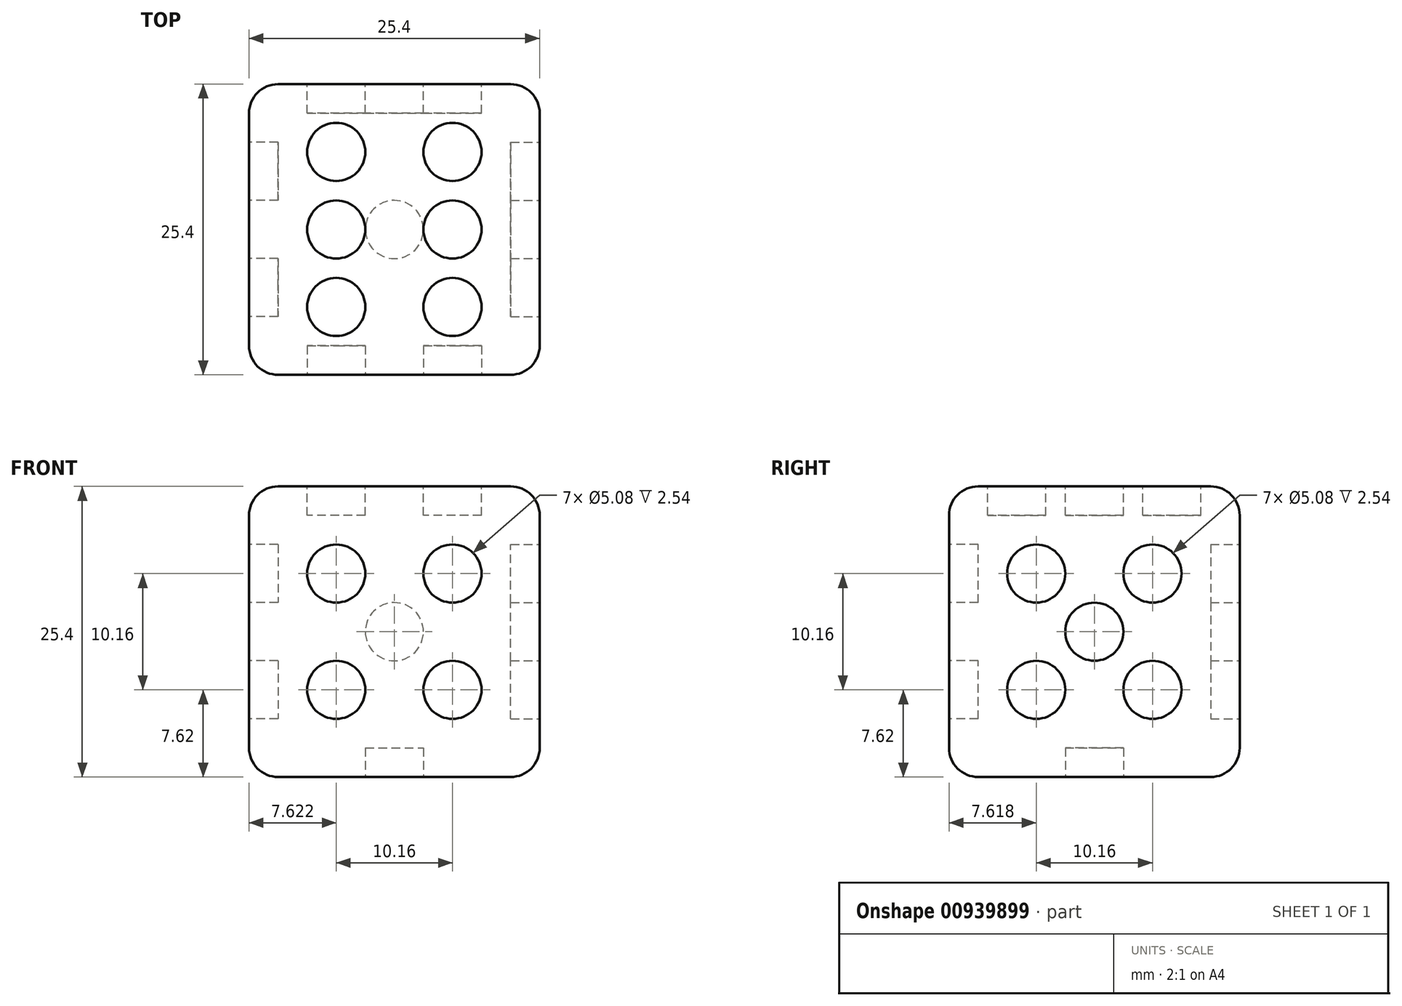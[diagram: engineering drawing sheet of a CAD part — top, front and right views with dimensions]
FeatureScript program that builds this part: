
annotation { "Feature Type Name" : "Feature", "Feature Type Description" : "" }
export const myFeature = defineFeature(function(context is Context, id is Id, definition is map)
    precondition{}
    {
        {
            var Q0;
            Q0=qCreatedBy(makeId("Top.planeOp"),FACE);
            var sketch = newSketch(context, id + "F0", { "sketchPlane" : qUnion([Q0])});
            skLineSegment(sketch, "E0.bottom", {"start": v(-52.85, 44.08) * mm, "end": v(-27.45, 44.08) * mm});
            skLineSegment(sketch, "E0.top", {"start": v(-52.85, 18.68) * mm, "end": v(-27.45, 18.68) * mm});
            skLineSegment(sketch, "E0.left", {"start": v(-52.85, 44.08) * mm, "end": v(-52.85, 18.68) * mm});
            skLineSegment(sketch, "E0.right", {"start": v(-27.45, 44.08) * mm, "end": v(-27.45, 18.68) * mm});
            skSolve(sketch);
        }
        {
            var Q0;
            Q0=makeQuery(id+"F0.imprint","IMPRINT",FACE,{"disambiguationData":[TD([[makeQuery(id+"F0.imprint","IMPRINT",EDGE,{"derivedFrom":sQuery(id+"F0.wireOp",EDGE,"E0.bottom")}),-1.0]])]});
            extrude(context, id + "F1", {"entities" : qUnion([Q0]), "depth" : 12.7 * mm, "offsetDistance" : 25.4 * mm});
        }
        {
            var Q0;
            Q0=makeQuery(id+"F1.opExtrude","CAP_FACE",FACE,{"disambiguationData":[OSD([sQuery(id+"F0.wireOp",EDGE,"E0.bottom"),sQuery(id+"F0.wireOp",EDGE,"E0.top"),sQuery(id+"F0.wireOp",EDGE,"E0.left"),sQuery(id+"F0.wireOp",EDGE,"E0.right")])],"isStart":false});
            var sketch = newSketch(context, id + "F2", { "sketchPlane" : qUnion([Q0])});
            skLineSegment(sketch, "E1.bottom", {"start": v(-49.04, 40.27) * mm, "end": v(-31.26, 40.27) * mm});
            skLineSegment(sketch, "E1.top", {"start": v(-49.04, 22.49) * mm, "end": v(-31.26, 22.49) * mm});
            skLineSegment(sketch, "E1.left", {"start": v(-49.04, 40.27) * mm, "end": v(-49.04, 22.49) * mm});
            skLineSegment(sketch, "E1.right", {"start": v(-31.26, 40.27) * mm, "end": v(-31.26, 22.49) * mm});
            skLineSegment(sketch, "E2.bottom", {"start": v(-52.85, 44.08) * mm, "end": v(-27.45, 44.08) * mm});
            skLineSegment(sketch, "E2.top", {"start": v(-52.85, 18.68) * mm, "end": v(-27.45, 18.68) * mm});
            skLineSegment(sketch, "E2.left", {"start": v(-52.85, 44.08) * mm, "end": v(-52.85, 18.68) * mm});
            skLineSegment(sketch, "E2.right", {"start": v(-27.45, 44.08) * mm, "end": v(-27.45, 18.68) * mm});
            skSolve(sketch);
        }
        {
            var Q0;
            Q0=makeQuery(id+"F2.imprint","IMPRINT",FACE,{"disambiguationData":[TD([[makeQuery(id+"F2.imprint","IMPRINT",EDGE,{"derivedFrom":sQuery(id+"F2.wireOp",EDGE,"E1.bottom")}),1.0]])]});
            var Q1;
            Q1=makeQuery(id+"F2.imprint","IMPRINT",FACE,{"disambiguationData":[TD([[makeQuery(id+"F2.imprint","IMPRINT",EDGE,{"derivedFrom":sQuery(id+"F2.wireOp",EDGE,"E1.bottom")}),-1.0]])]});
            extrude(context, id + "F3", {"entities" : qUnion([Q0, Q1]), "operationType" : NewBodyOperationType.ADD, "depth" : 8.9 * mm, "offsetDistance" : 25.4 * mm});
        }
        {
            var Q0;
            Q0=makeQuery(id+"F3.opExtrude","CAP_FACE",FACE,{"disambiguationData":[OSD([sQuery(id+"F2.wireOp",EDGE,"E1.bottom"),sQuery(id+"F2.wireOp",EDGE,"E1.top"),sQuery(id+"F2.wireOp",EDGE,"E1.left"),sQuery(id+"F2.wireOp",EDGE,"E1.right"),sQuery(id+"F2.wireOp",EDGE,"E2.bottom"),sQuery(id+"F2.wireOp",EDGE,"E2.top"),sQuery(id+"F2.wireOp",EDGE,"E2.left"),sQuery(id+"F2.wireOp",EDGE,"E2.right")])],"isStart":false});
            var sketch = newSketch(context, id + "F4", { "sketchPlane" : qUnion([Q0])});
            skLineSegment(sketch, "E3.bottom", {"start": v(-52.85, 44.08) * mm, "end": v(-27.45, 44.08) * mm});
            skLineSegment(sketch, "E3.top", {"start": v(-52.85, 18.68) * mm, "end": v(-27.45, 18.68) * mm});
            skLineSegment(sketch, "E3.left", {"start": v(-52.85, 44.08) * mm, "end": v(-52.85, 18.68) * mm});
            skLineSegment(sketch, "E3.right", {"start": v(-27.45, 44.08) * mm, "end": v(-27.45, 18.68) * mm});
            skSolve(sketch);
        }
        {
            var Q0;
            Q0=qSketchRegion(id+"F4",true);
            extrude(context, id + "F5", {"entities" : qUnion([Q0]), "operationType" : NewBodyOperationType.ADD, "depth" : 3.8 * mm, "offsetDistance" : 25.4 * mm});
        }
        {
            var Q0;
            Q0=makeQuery(id+"F5.opExtrude","CAP_EDGE",EDGE,{"disambiguationData":[OSD([sQuery(id+"F4.wireOp",EDGE,"E3.top")])],"isStart":false});
            var Q1;
            Q1=makeQuery(id+"F5.opExtrude","CAP_EDGE",EDGE,{"disambiguationData":[OSD([sQuery(id+"F4.wireOp",EDGE,"E3.right")])],"isStart":false});
            var Q2;
            Q2=makeQuery(id+"F5.boolean.opBoolean","MERGE",EDGE,{"derivedFrom":[makeQuery(id+"F3.boolean.opBoolean","MERGE",EDGE,{"derivedFrom":[makeQuery(id+"F1.opExtrude","SWEPT_EDGE",EDGE,{"disambiguationData":[OSD([sQuery(id+"F0.wireOp",EDGE,"E0.top"),sQuery(id+"F0.wireOp",EDGE,"E0.right")])]}),makeQuery(id+"F3.opExtrude","SWEPT_EDGE",EDGE,{"disambiguationData":[OSD([sQuery(id+"F2.wireOp",EDGE,"E2.top"),sQuery(id+"F2.wireOp",EDGE,"E2.right")])]})]}),makeQuery(id+"F5.opExtrude","SWEPT_EDGE",EDGE,{"disambiguationData":[OSD([sQuery(id+"F4.wireOp",EDGE,"E3.top"),sQuery(id+"F4.wireOp",EDGE,"E3.right")])]})]});
            var Q3;
            Q3=makeQuery(id+"F5.boolean.opBoolean","MERGE",EDGE,{"derivedFrom":[makeQuery(id+"F3.boolean.opBoolean","MERGE",EDGE,{"derivedFrom":[makeQuery(id+"F1.opExtrude","SWEPT_EDGE",EDGE,{"disambiguationData":[OSD([sQuery(id+"F0.wireOp",EDGE,"E0.bottom"),sQuery(id+"F0.wireOp",EDGE,"E0.right")])]}),makeQuery(id+"F3.opExtrude","SWEPT_EDGE",EDGE,{"disambiguationData":[OSD([sQuery(id+"F2.wireOp",EDGE,"E2.bottom"),sQuery(id+"F2.wireOp",EDGE,"E2.right")])]})]}),makeQuery(id+"F5.opExtrude","SWEPT_EDGE",EDGE,{"disambiguationData":[OSD([sQuery(id+"F4.wireOp",EDGE,"E3.bottom"),sQuery(id+"F4.wireOp",EDGE,"E3.right")])]})]});
            var Q4;
            Q4=makeQuery(id+"F5.opExtrude","CAP_EDGE",EDGE,{"disambiguationData":[OSD([sQuery(id+"F4.wireOp",EDGE,"E3.bottom")])],"isStart":false});
            var Q5;
            Q5=makeQuery(id+"F5.opExtrude","CAP_EDGE",EDGE,{"disambiguationData":[OSD([sQuery(id+"F4.wireOp",EDGE,"E3.left")])],"isStart":false});
            var Q6;
            Q6=makeQuery(id+"F5.boolean.opBoolean","MERGE",EDGE,{"derivedFrom":[makeQuery(id+"F3.boolean.opBoolean","MERGE",EDGE,{"derivedFrom":[makeQuery(id+"F1.opExtrude","SWEPT_EDGE",EDGE,{"disambiguationData":[OSD([sQuery(id+"F0.wireOp",EDGE,"E0.top"),sQuery(id+"F0.wireOp",EDGE,"E0.left")])]}),makeQuery(id+"F3.opExtrude","SWEPT_EDGE",EDGE,{"disambiguationData":[OSD([sQuery(id+"F2.wireOp",EDGE,"E2.top"),sQuery(id+"F2.wireOp",EDGE,"E2.left")])]})]}),makeQuery(id+"F5.opExtrude","SWEPT_EDGE",EDGE,{"disambiguationData":[OSD([sQuery(id+"F4.wireOp",EDGE,"E3.top"),sQuery(id+"F4.wireOp",EDGE,"E3.left")])]})]});
            var Q7;
            Q7=makeQuery(id+"F1.opExtrude","CAP_EDGE",EDGE,{"disambiguationData":[OSD([sQuery(id+"F0.wireOp",EDGE,"E0.top")])],"isStart":true});
            var Q8;
            Q8=makeQuery(id+"F1.opExtrude","CAP_EDGE",EDGE,{"disambiguationData":[OSD([sQuery(id+"F0.wireOp",EDGE,"E0.left")])],"isStart":true});
            var Q9;
            Q9=makeQuery(id+"F1.opExtrude","CAP_EDGE",EDGE,{"disambiguationData":[OSD([sQuery(id+"F0.wireOp",EDGE,"E0.bottom")])],"isStart":true});
            var Q10;
            Q10=makeQuery(id+"F1.opExtrude","CAP_EDGE",EDGE,{"disambiguationData":[OSD([sQuery(id+"F0.wireOp",EDGE,"E0.right")])],"isStart":true});
            var Q11;
            Q11=makeQuery(id+"F5.boolean.opBoolean","MERGE",EDGE,{"derivedFrom":[makeQuery(id+"F3.boolean.opBoolean","MERGE",EDGE,{"derivedFrom":[makeQuery(id+"F1.opExtrude","SWEPT_EDGE",EDGE,{"disambiguationData":[OSD([sQuery(id+"F0.wireOp",EDGE,"E0.bottom"),sQuery(id+"F0.wireOp",EDGE,"E0.left")])]}),makeQuery(id+"F3.opExtrude","SWEPT_EDGE",EDGE,{"disambiguationData":[OSD([sQuery(id+"F2.wireOp",EDGE,"E2.bottom"),sQuery(id+"F2.wireOp",EDGE,"E2.left")])]})]}),makeQuery(id+"F5.opExtrude","SWEPT_EDGE",EDGE,{"disambiguationData":[OSD([sQuery(id+"F4.wireOp",EDGE,"E3.bottom"),sQuery(id+"F4.wireOp",EDGE,"E3.left")])]})]});
            fillet(context, id + "F6", {"entities" : qUnion([Q0, Q1, Q2, Q3, Q4, Q5, Q6, Q7, Q8, Q9, Q10, Q11]), "radius" : 2.54 * mm, "tangentPropagation" : true, "allowEdgeOverflow" : false});
        }
        {
            var Q0;
            Q0=makeQuery(id+"F5.opExtrude","CAP_FACE",FACE,{"disambiguationData":[OSD([sQuery(id+"F4.wireOp",EDGE,"E3.bottom"),sQuery(id+"F4.wireOp",EDGE,"E3.top"),sQuery(id+"F4.wireOp",EDGE,"E3.left"),sQuery(id+"F4.wireOp",EDGE,"E3.right")])],"isStart":false});
            var sketch = newSketch(context, id + "F7", { "sketchPlane" : qUnion([Q0])});
            skLineSegment(sketch, "E4", {"start": v(-50.3, 41.54) * mm, "end": v(-45.23, 41.54) * mm});
            skLineSegment(sketch, "E5", {"start": v(-29.99, 41.54) * mm, "end": v(-29.99, 38.15) * mm});
            skLineSegment(sketch, "E6", {"start": v(-29.99, 21.22) * mm, "end": v(-35.07, 21.22) * mm});
            skLineSegment(sketch, "E7", {"start": v(-50.3, 21.22) * mm, "end": v(-50.3, 24.6) * mm});
            skLineSegment(sketch, "E8", {"start": v(-50.3, 24.6) * mm, "end": v(-45.23, 24.6) * mm});
            skLineSegment(sketch, "E9", {"start": v(-45.23, 41.54) * mm, "end": v(-45.23, 38.15) * mm});
            skLineSegment(sketch, "E10", {"start": v(-29.99, 38.15) * mm, "end": v(-35.07, 38.15) * mm});
            skLineSegment(sketch, "E11", {"start": v(-35.07, 21.22) * mm, "end": v(-35.07, 24.6) * mm});
            skLineSegment(sketch, "E12", {"start": v(-45.23, 38.15) * mm, "end": v(-45.23, 31.38) * mm});
            skLineSegment(sketch, "E13", {"start": v(-35.07, 38.15) * mm, "end": v(-35.07, 31.38) * mm});
            skCircle(sketch, "E14", {"center": v(-45.23, 38.15) * mm, "radius": 2.54 * mm});
            skCircle(sketch, "E15", {"center": v(-45.23, 31.38) * mm, "radius": 2.54 * mm});
            skCircle(sketch, "E16", {"center": v(-45.23, 24.6) * mm, "radius": 2.54 * mm});
            skCircle(sketch, "E17", {"center": v(-35.07, 24.6) * mm, "radius": 2.54 * mm});
            skCircle(sketch, "E18", {"center": v(-35.07, 31.38) * mm, "radius": 2.54 * mm});
            skCircle(sketch, "E19", {"center": v(-35.07, 38.15) * mm, "radius": 2.54 * mm});
            skSolve(sketch);
        }
        {
            var Q0;
            {var subQ0=sQuery(id+"F7.wireOp",EDGE,"E12");var subQ1=sQuery(id+"F7.wireOp",EDGE,"E9");var subQ2=makeQuery(id+"F7.imprint","INTERSECT",VERTEX,{"derivedFrom":[subQ1,subQ0]});Q0=makeQuery(id+"F7.imprint","IMPRINT",FACE,{"disambiguationData":[TD([[makeQuery(id+"F7.imprint","IMPRINT",EDGE,{"disambiguationData":[TD([[subQ2,1.0]])],"derivedFrom":subQ1}),1.0]])]});}
            var Q1;
            {var subQ0=sQuery(id+"F7.wireOp",EDGE,"E12");var subQ1=sQuery(id+"F7.wireOp",EDGE,"E9");var subQ2=makeQuery(id+"F7.imprint","INTERSECT",VERTEX,{"derivedFrom":[subQ1,subQ0]});Q1=makeQuery(id+"F7.imprint","IMPRINT",FACE,{"disambiguationData":[TD([[makeQuery(id+"F7.imprint","IMPRINT",EDGE,{"disambiguationData":[TD([[subQ2,1.0]])],"derivedFrom":subQ1}),-1.0]])]});}
            var Q2;
            {var subQ0=sQuery(id+"F7.wireOp",EDGE,"E13");var subQ1=sQuery(id+"F7.wireOp",EDGE,"E10");var subQ2=makeQuery(id+"F7.imprint","INTERSECT",VERTEX,{"derivedFrom":[subQ1,subQ0]});Q2=makeQuery(id+"F7.imprint","IMPRINT",FACE,{"disambiguationData":[TD([[makeQuery(id+"F7.imprint","IMPRINT",EDGE,{"disambiguationData":[TD([[subQ2,1.0]])],"derivedFrom":subQ1}),-1.0]])]});}
            var Q3;
            {var subQ0=sQuery(id+"F7.wireOp",EDGE,"E13");var subQ1=sQuery(id+"F7.wireOp",EDGE,"E10");var subQ2=makeQuery(id+"F7.imprint","INTERSECT",VERTEX,{"derivedFrom":[subQ1,subQ0]});Q3=makeQuery(id+"F7.imprint","IMPRINT",FACE,{"disambiguationData":[TD([[makeQuery(id+"F7.imprint","IMPRINT",EDGE,{"disambiguationData":[TD([[subQ2,1.0]])],"derivedFrom":subQ1}),1.0]])]});}
            var Q4;
            Q4=makeQuery(id+"F7.imprint","IMPRINT",FACE,{"disambiguationData":[TD([[makeQuery(id+"F7.imprint","IMPRINT",EDGE,{"derivedFrom":sQuery(id+"F7.wireOp",EDGE,"E18")}),1.0]])]});
            var Q5;
            Q5=makeQuery(id+"F7.imprint","IMPRINT",FACE,{"disambiguationData":[TD([[makeQuery(id+"F7.imprint","IMPRINT",EDGE,{"derivedFrom":sQuery(id+"F7.wireOp",EDGE,"E17")}),1.0]])]});
            var Q6;
            Q6=makeQuery(id+"F7.imprint","IMPRINT",FACE,{"disambiguationData":[TD([[makeQuery(id+"F7.imprint","IMPRINT",EDGE,{"derivedFrom":sQuery(id+"F7.wireOp",EDGE,"E16")}),1.0]])]});
            var Q7;
            Q7=makeQuery(id+"F7.imprint","IMPRINT",FACE,{"disambiguationData":[TD([[makeQuery(id+"F7.imprint","IMPRINT",EDGE,{"derivedFrom":sQuery(id+"F7.wireOp",EDGE,"E15")}),1.0]])]});
            extrude(context, id + "F8", {"entities" : qUnion([Q0, Q1, Q2, Q3, Q4, Q5, Q6, Q7]), "operationType" : NewBodyOperationType.REMOVE, "oppositeDirection" : true, "depth" : 2.54 * mm, "offsetDistance" : 25.4 * mm});
        }
        {
            var Q0;
            Q0=makeQuery(id+"F5.boolean.opBoolean","MERGE",FACE,{"derivedFrom":[makeQuery(id+"F3.boolean.opBoolean","MERGE",FACE,{"derivedFrom":[makeQuery(id+"F1.opExtrude","SWEPT_FACE",FACE,{"disambiguationData":[OSD([sQuery(id+"F0.wireOp",EDGE,"E0.right")])]}),makeQuery(id+"F3.opExtrude","SWEPT_FACE",FACE,{"disambiguationData":[OSD([sQuery(id+"F2.wireOp",EDGE,"E2.right")])]})]}),makeQuery(id+"F5.opExtrude","SWEPT_FACE",FACE,{"disambiguationData":[OSD([sQuery(id+"F4.wireOp",EDGE,"E3.right")])]})]});
            var sketch = newSketch(context, id + "F9", { "sketchPlane" : qUnion([Q0])});
            skLineSegment(sketch, "E20", {"start": v(21.22, 22.86) * mm, "end": v(31.38, 22.86) * mm});
            skLineSegment(sketch, "E21", {"start": v(41.54, 22.86) * mm, "end": v(41.54, 12.7) * mm});
            skLineSegment(sketch, "E22", {"start": v(41.54, 12.7) * mm, "end": v(31.38, 12.7) * mm});
            skCircle(sketch, "E23", {"center": v(31.38, 12.7) * mm, "radius": 2.54 * mm});
            skLineSegment(sketch, "E24", {"start": v(21.22, 22.86) * mm, "end": v(26.3, 22.86) * mm});
            skLineSegment(sketch, "E25", {"start": v(26.3, 22.86) * mm, "end": v(26.3, 17.78) * mm});
            skCircle(sketch, "E26", {"center": v(26.3, 17.78) * mm, "radius": 2.54 * mm});
            skLineSegment(sketch, "E27", {"start": v(26.3, 17.78) * mm, "end": v(26.3, 7.62) * mm});
            skCircle(sketch, "E28", {"center": v(26.3, 7.62) * mm, "radius": 2.54 * mm});
            skLineSegment(sketch, "E29", {"start": v(41.54, 22.86) * mm, "end": v(41.54, 17.78) * mm});
            skLineSegment(sketch, "E30", {"start": v(41.54, 17.78) * mm, "end": v(36.46, 17.78) * mm});
            skCircle(sketch, "E31", {"center": v(36.46, 17.78) * mm, "radius": 2.54 * mm});
            skLineSegment(sketch, "E32", {"start": v(36.46, 17.78) * mm, "end": v(36.46, 7.62) * mm});
            skCircle(sketch, "E33", {"center": v(36.46, 7.62) * mm, "radius": 2.54 * mm});
            skSolve(sketch);
        }
        {
            var Q0;
            {var subQ0=sQuery(id+"F9.wireOp",EDGE,"E27");var subQ1=sQuery(id+"F9.wireOp",EDGE,"E25");var subQ2=makeQuery(id+"F9.imprint","INTERSECT",VERTEX,{"derivedFrom":[subQ1,subQ0]});Q0=makeQuery(id+"F9.imprint","IMPRINT",FACE,{"disambiguationData":[TD([[makeQuery(id+"F9.imprint","IMPRINT",EDGE,{"disambiguationData":[TD([[subQ2,1.0]])],"derivedFrom":subQ1}),1.0]])]});}
            var Q1;
            {var subQ0=sQuery(id+"F9.wireOp",EDGE,"E27");var subQ1=sQuery(id+"F9.wireOp",EDGE,"E25");var subQ2=makeQuery(id+"F9.imprint","INTERSECT",VERTEX,{"derivedFrom":[subQ1,subQ0]});Q1=makeQuery(id+"F9.imprint","IMPRINT",FACE,{"disambiguationData":[TD([[makeQuery(id+"F9.imprint","IMPRINT",EDGE,{"disambiguationData":[TD([[subQ2,1.0]])],"derivedFrom":subQ1}),-1.0]])]});}
            var Q2;
            Q2=makeQuery(id+"F9.imprint","IMPRINT",FACE,{"disambiguationData":[TD([[makeQuery(id+"F9.imprint","IMPRINT",EDGE,{"derivedFrom":sQuery(id+"F9.wireOp",EDGE,"E28")}),1.0]])]});
            var Q3;
            Q3=makeQuery(id+"F9.imprint","IMPRINT",FACE,{"disambiguationData":[TD([[makeQuery(id+"F9.imprint","IMPRINT",EDGE,{"derivedFrom":sQuery(id+"F9.wireOp",EDGE,"E23")}),1.0]])]});
            var Q4;
            {var subQ0=sQuery(id+"F9.wireOp",EDGE,"E32");var subQ1=sQuery(id+"F9.wireOp",EDGE,"E30");var subQ2=makeQuery(id+"F9.imprint","INTERSECT",VERTEX,{"derivedFrom":[subQ1,subQ0]});Q4=makeQuery(id+"F9.imprint","IMPRINT",FACE,{"disambiguationData":[TD([[makeQuery(id+"F9.imprint","IMPRINT",EDGE,{"disambiguationData":[TD([[subQ2,1.0]])],"derivedFrom":subQ1}),-1.0]])]});}
            var Q5;
            {var subQ0=sQuery(id+"F9.wireOp",EDGE,"E32");var subQ1=sQuery(id+"F9.wireOp",EDGE,"E30");var subQ2=makeQuery(id+"F9.imprint","INTERSECT",VERTEX,{"derivedFrom":[subQ1,subQ0]});Q5=makeQuery(id+"F9.imprint","IMPRINT",FACE,{"disambiguationData":[TD([[makeQuery(id+"F9.imprint","IMPRINT",EDGE,{"disambiguationData":[TD([[subQ2,1.0]])],"derivedFrom":subQ1}),1.0]])]});}
            var Q6;
            Q6=makeQuery(id+"F9.imprint","IMPRINT",FACE,{"disambiguationData":[TD([[makeQuery(id+"F9.imprint","IMPRINT",EDGE,{"derivedFrom":sQuery(id+"F9.wireOp",EDGE,"E33")}),1.0]])]});
            extrude(context, id + "F10", {"entities" : qUnion([Q0, Q1, Q2, Q3, Q4, Q5, Q6]), "operationType" : NewBodyOperationType.REMOVE, "oppositeDirection" : true, "depth" : 2.54 * mm, "offsetDistance" : 25.4 * mm});
        }
        {
            var Q0;
            Q0=makeQuery(id+"F5.boolean.opBoolean","MERGE",FACE,{"derivedFrom":[makeQuery(id+"F3.boolean.opBoolean","MERGE",FACE,{"derivedFrom":[makeQuery(id+"F1.opExtrude","SWEPT_FACE",FACE,{"disambiguationData":[OSD([sQuery(id+"F0.wireOp",EDGE,"E0.bottom")])]}),makeQuery(id+"F3.opExtrude","SWEPT_FACE",FACE,{"disambiguationData":[OSD([sQuery(id+"F2.wireOp",EDGE,"E2.bottom")])]})]}),makeQuery(id+"F5.opExtrude","SWEPT_FACE",FACE,{"disambiguationData":[OSD([sQuery(id+"F4.wireOp",EDGE,"E3.bottom")])]})]});
            var sketch = newSketch(context, id + "F11", { "sketchPlane" : qUnion([Q0])});
            skLineSegment(sketch, "E34", {"start": v(29.99, 22.86) * mm, "end": v(40.15, 22.86) * mm});
            skLineSegment(sketch, "E35", {"start": v(40.15, 22.86) * mm, "end": v(40.15, 12.7) * mm});
            skCircle(sketch, "E36", {"center": v(40.15, 12.7) * mm, "radius": 2.54 * mm});
            skLineSegment(sketch, "E37", {"start": v(29.99, 22.86) * mm, "end": v(35.07, 22.86) * mm});
            skLineSegment(sketch, "E38", {"start": v(35.07, 22.86) * mm, "end": v(35.07, 17.78) * mm});
            skLineSegment(sketch, "E39", {"start": v(50.3, 2.54) * mm, "end": v(45.23, 2.54) * mm});
            skLineSegment(sketch, "E40", {"start": v(45.23, 2.54) * mm, "end": v(45.23, 7.62) * mm});
            skCircle(sketch, "E41", {"center": v(35.07, 17.78) * mm, "radius": 2.54 * mm});
            skCircle(sketch, "E42", {"center": v(45.23, 7.62) * mm, "radius": 2.54 * mm});
            skSolve(sketch);
        }
        {
            var Q0;
            Q0=makeQuery(id+"F11.imprint","IMPRINT",FACE,{"disambiguationData":[TD([[makeQuery(id+"F11.imprint","IMPRINT",EDGE,{"derivedFrom":sQuery(id+"F11.wireOp",EDGE,"E41")}),1.0]])]});
            var Q1;
            Q1=makeQuery(id+"F11.imprint","IMPRINT",FACE,{"disambiguationData":[TD([[makeQuery(id+"F11.imprint","IMPRINT",EDGE,{"derivedFrom":sQuery(id+"F11.wireOp",EDGE,"E36")}),1.0]])]});
            var Q2;
            Q2=makeQuery(id+"F11.imprint","IMPRINT",FACE,{"disambiguationData":[TD([[makeQuery(id+"F11.imprint","IMPRINT",EDGE,{"derivedFrom":sQuery(id+"F11.wireOp",EDGE,"E42")}),1.0]])]});
            extrude(context, id + "F12", {"entities" : qUnion([Q0, Q1, Q2]), "operationType" : NewBodyOperationType.REMOVE, "oppositeDirection" : true, "depth" : 2.54 * mm, "offsetDistance" : 25.4 * mm});
        }
        {
            var Q0;
            Q0=makeQuery(id+"F5.boolean.opBoolean","MERGE",FACE,{"derivedFrom":[makeQuery(id+"F3.boolean.opBoolean","MERGE",FACE,{"derivedFrom":[makeQuery(id+"F1.opExtrude","SWEPT_FACE",FACE,{"disambiguationData":[OSD([sQuery(id+"F0.wireOp",EDGE,"E0.left")])]}),makeQuery(id+"F3.opExtrude","SWEPT_FACE",FACE,{"disambiguationData":[OSD([sQuery(id+"F2.wireOp",EDGE,"E2.left")])]})]}),makeQuery(id+"F5.opExtrude","SWEPT_FACE",FACE,{"disambiguationData":[OSD([sQuery(id+"F4.wireOp",EDGE,"E3.left")])]})]});
            var sketch = newSketch(context, id + "F13", { "sketchPlane" : qUnion([Q0])});
            skLineSegment(sketch, "E43", {"start": v(-41.54, 22.86) * mm, "end": v(-36.46, 22.86) * mm});
            skLineSegment(sketch, "E44", {"start": v(-36.46, 22.86) * mm, "end": v(-36.46, 17.78) * mm});
            skLineSegment(sketch, "E45", {"start": v(-21.22, 2.54) * mm, "end": v(-26.3, 2.54) * mm});
            skLineSegment(sketch, "E46", {"start": v(-26.3, 2.54) * mm, "end": v(-26.3, 7.62) * mm});
            skCircle(sketch, "E47", {"center": v(-36.46, 17.78) * mm, "radius": 2.54 * mm});
            skCircle(sketch, "E48", {"center": v(-26.3, 7.62) * mm, "radius": 2.54 * mm});
            skSolve(sketch);
        }
        {
            var Q0;
            Q0=makeQuery(id+"F13.imprint","IMPRINT",FACE,{"disambiguationData":[TD([[makeQuery(id+"F13.imprint","IMPRINT",EDGE,{"derivedFrom":sQuery(id+"F13.wireOp",EDGE,"E47")}),1.0]])]});
            var Q1;
            Q1=makeQuery(id+"F13.imprint","IMPRINT",FACE,{"disambiguationData":[TD([[makeQuery(id+"F13.imprint","IMPRINT",EDGE,{"derivedFrom":sQuery(id+"F13.wireOp",EDGE,"E48")}),1.0]])]});
            extrude(context, id + "F14", {"entities" : qUnion([Q0, Q1]), "operationType" : NewBodyOperationType.REMOVE, "oppositeDirection" : true, "depth" : 2.54 * mm, "offsetDistance" : 25.4 * mm});
        }
        {
            var Q0;
            Q0=makeQuery(id+"F5.boolean.opBoolean","MERGE",FACE,{"derivedFrom":[makeQuery(id+"F3.boolean.opBoolean","MERGE",FACE,{"derivedFrom":[makeQuery(id+"F1.opExtrude","SWEPT_FACE",FACE,{"disambiguationData":[OSD([sQuery(id+"F0.wireOp",EDGE,"E0.top")])]}),makeQuery(id+"F3.opExtrude","SWEPT_FACE",FACE,{"disambiguationData":[OSD([sQuery(id+"F2.wireOp",EDGE,"E2.top")])]})]}),makeQuery(id+"F5.opExtrude","SWEPT_FACE",FACE,{"disambiguationData":[OSD([sQuery(id+"F4.wireOp",EDGE,"E3.top")])]})]});
            var sketch = newSketch(context, id + "F15", { "sketchPlane" : qUnion([Q0])});
            skLineSegment(sketch, "E49", {"start": v(-50.3, 22.86) * mm, "end": v(-45.23, 22.86) * mm});
            skLineSegment(sketch, "E50", {"start": v(-45.23, 22.86) * mm, "end": v(-45.23, 17.78) * mm});
            skLineSegment(sketch, "E51", {"start": v(-29.99, 22.86) * mm, "end": v(-29.99, 17.78) * mm});
            skLineSegment(sketch, "E52", {"start": v(-29.99, 17.78) * mm, "end": v(-35.07, 17.78) * mm});
            skLineSegment(sketch, "E53", {"start": v(-29.99, 2.54) * mm, "end": v(-35.07, 2.54) * mm});
            skLineSegment(sketch, "E54", {"start": v(-35.07, 2.54) * mm, "end": v(-35.07, 7.62) * mm});
            skLineSegment(sketch, "E55", {"start": v(-50.3, 2.54) * mm, "end": v(-45.23, 2.54) * mm});
            skLineSegment(sketch, "E56", {"start": v(-45.23, 2.54) * mm, "end": v(-45.23, 7.62) * mm});
            skCircle(sketch, "E57", {"center": v(-45.23, 17.78) * mm, "radius": 2.54 * mm});
            skCircle(sketch, "E58", {"center": v(-35.07, 17.78) * mm, "radius": 2.54 * mm});
            skCircle(sketch, "E59", {"center": v(-35.07, 7.62) * mm, "radius": 2.54 * mm});
            skCircle(sketch, "E60", {"center": v(-45.23, 7.62) * mm, "radius": 2.54 * mm});
            skSolve(sketch);
        }
        {
            var Q0;
            Q0=makeQuery(id+"F15.imprint","IMPRINT",FACE,{"disambiguationData":[TD([[makeQuery(id+"F15.imprint","IMPRINT",EDGE,{"derivedFrom":sQuery(id+"F15.wireOp",EDGE,"E57")}),1.0]])]});
            var Q1;
            Q1=makeQuery(id+"F15.imprint","IMPRINT",FACE,{"disambiguationData":[TD([[makeQuery(id+"F15.imprint","IMPRINT",EDGE,{"derivedFrom":sQuery(id+"F15.wireOp",EDGE,"E58")}),1.0]])]});
            var Q2;
            Q2=makeQuery(id+"F15.imprint","IMPRINT",FACE,{"disambiguationData":[TD([[makeQuery(id+"F15.imprint","IMPRINT",EDGE,{"derivedFrom":sQuery(id+"F15.wireOp",EDGE,"E59")}),1.0]])]});
            var Q3;
            Q3=makeQuery(id+"F15.imprint","IMPRINT",FACE,{"disambiguationData":[TD([[makeQuery(id+"F15.imprint","IMPRINT",EDGE,{"derivedFrom":sQuery(id+"F15.wireOp",EDGE,"E60")}),1.0]])]});
            extrude(context, id + "F16", {"entities" : qUnion([Q0, Q1, Q2, Q3]), "operationType" : NewBodyOperationType.REMOVE, "oppositeDirection" : true, "depth" : 2.54 * mm, "offsetDistance" : 25.4 * mm});
        }
        {
            var Q0;
            Q0=makeQuery(id+"F1.opExtrude","CAP_FACE",FACE,{"disambiguationData":[OSD([sQuery(id+"F0.wireOp",EDGE,"E0.bottom"),sQuery(id+"F0.wireOp",EDGE,"E0.top"),sQuery(id+"F0.wireOp",EDGE,"E0.left"),sQuery(id+"F0.wireOp",EDGE,"E0.right")])],"isStart":true});
            var sketch = newSketch(context, id + "F17", { "sketchPlane" : qUnion([Q0])});
            skLineSegment(sketch, "E61", {"start": v(-50.3, -21.22) * mm, "end": v(-40.15, -21.22) * mm});
            skLineSegment(sketch, "E62", {"start": v(-29.99, -21.22) * mm, "end": v(-29.99, -31.38) * mm});
            skLineSegment(sketch, "E63", {"start": v(-40.15, -21.22) * mm, "end": v(-40.15, -31.38) * mm});
            skCircle(sketch, "E64", {"center": v(-40.15, -31.38) * mm, "radius": 2.54 * mm});
            skSolve(sketch);
        }
        {
            var Q0;
            Q0=makeQuery(id+"F17.imprint","IMPRINT",FACE,{"disambiguationData":[TD([[makeQuery(id+"F17.imprint","IMPRINT",EDGE,{"derivedFrom":sQuery(id+"F17.wireOp",EDGE,"E64")}),1.0]])]});
            extrude(context, id + "F18", {"entities" : qUnion([Q0]), "operationType" : NewBodyOperationType.REMOVE, "oppositeDirection" : true, "depth" : 2.54 * mm, "offsetDistance" : 25.4 * mm});
        }
        {
            var Q0;
            Q0=makeQuery(id+"F11.imprint","IMPRINT",FACE,{"disambiguationData":[TD([[makeQuery(id+"F11.imprint","IMPRINT",EDGE,{"derivedFrom":sQuery(id+"F11.wireOp",EDGE,"E41")}),1.0]])]});
            var Q1;
            Q1=makeQuery(id+"F11.imprint","IMPRINT",FACE,{"disambiguationData":[TD([[makeQuery(id+"F11.imprint","IMPRINT",EDGE,{"derivedFrom":sQuery(id+"F11.wireOp",EDGE,"E36")}),1.0]])]});
            var Q2;
            Q2=makeQuery(id+"F11.imprint","IMPRINT",FACE,{"disambiguationData":[TD([[makeQuery(id+"F11.imprint","IMPRINT",EDGE,{"derivedFrom":sQuery(id+"F11.wireOp",EDGE,"E42")}),1.0]])]});
            extrude(context, id + "F19", {"entities" : qUnion([Q0, Q1, Q2]), "oppositeDirection" : true, "depth" : 2.54 * mm, "offsetDistance" : 25.4 * mm});
        }
        {
            var Q0;
            {var subQ0=sQuery(id+"F9.wireOp",EDGE,"E27");var subQ1=sQuery(id+"F9.wireOp",EDGE,"E25");var subQ2=makeQuery(id+"F9.imprint","INTERSECT",VERTEX,{"derivedFrom":[subQ1,subQ0]});Q0=makeQuery(id+"F9.imprint","IMPRINT",FACE,{"disambiguationData":[TD([[makeQuery(id+"F9.imprint","IMPRINT",EDGE,{"disambiguationData":[TD([[subQ2,1.0]])],"derivedFrom":subQ1}),1.0]])]});}
            var Q1;
            {var subQ0=sQuery(id+"F9.wireOp",EDGE,"E27");var subQ1=sQuery(id+"F9.wireOp",EDGE,"E25");var subQ2=makeQuery(id+"F9.imprint","INTERSECT",VERTEX,{"derivedFrom":[subQ1,subQ0]});Q1=makeQuery(id+"F9.imprint","IMPRINT",FACE,{"disambiguationData":[TD([[makeQuery(id+"F9.imprint","IMPRINT",EDGE,{"disambiguationData":[TD([[subQ2,1.0]])],"derivedFrom":subQ1}),-1.0]])]});}
            var Q2;
            {var subQ0=sQuery(id+"F9.wireOp",EDGE,"E32");var subQ1=sQuery(id+"F9.wireOp",EDGE,"E30");var subQ2=makeQuery(id+"F9.imprint","INTERSECT",VERTEX,{"derivedFrom":[subQ1,subQ0]});Q2=makeQuery(id+"F9.imprint","IMPRINT",FACE,{"disambiguationData":[TD([[makeQuery(id+"F9.imprint","IMPRINT",EDGE,{"disambiguationData":[TD([[subQ2,1.0]])],"derivedFrom":subQ1}),-1.0]])]});}
            var Q3;
            {var subQ0=sQuery(id+"F9.wireOp",EDGE,"E32");var subQ1=sQuery(id+"F9.wireOp",EDGE,"E30");var subQ2=makeQuery(id+"F9.imprint","INTERSECT",VERTEX,{"derivedFrom":[subQ1,subQ0]});Q3=makeQuery(id+"F9.imprint","IMPRINT",FACE,{"disambiguationData":[TD([[makeQuery(id+"F9.imprint","IMPRINT",EDGE,{"disambiguationData":[TD([[subQ2,1.0]])],"derivedFrom":subQ1}),1.0]])]});}
            var Q4;
            Q4=makeQuery(id+"F9.imprint","IMPRINT",FACE,{"disambiguationData":[TD([[makeQuery(id+"F9.imprint","IMPRINT",EDGE,{"derivedFrom":sQuery(id+"F9.wireOp",EDGE,"E28")}),1.0]])]});
            var Q5;
            Q5=makeQuery(id+"F9.imprint","IMPRINT",FACE,{"disambiguationData":[TD([[makeQuery(id+"F9.imprint","IMPRINT",EDGE,{"derivedFrom":sQuery(id+"F9.wireOp",EDGE,"E23")}),1.0]])]});
            var Q6;
            Q6=makeQuery(id+"F9.imprint","IMPRINT",FACE,{"disambiguationData":[TD([[makeQuery(id+"F9.imprint","IMPRINT",EDGE,{"derivedFrom":sQuery(id+"F9.wireOp",EDGE,"E33")}),1.0]])]});
            extrude(context, id + "F20", {"entities" : qUnion([Q0, Q1, Q2, Q3, Q4, Q5, Q6]), "oppositeDirection" : true, "depth" : 2.54 * mm, "offsetDistance" : 25.4 * mm});
        }
        {
            var Q0;
            Q0=makeQuery(id+"F13.imprint","IMPRINT",FACE,{"disambiguationData":[TD([[makeQuery(id+"F13.imprint","IMPRINT",EDGE,{"derivedFrom":sQuery(id+"F13.wireOp",EDGE,"E47")}),1.0]])]});
            var Q1;
            Q1=makeQuery(id+"F13.imprint","IMPRINT",FACE,{"disambiguationData":[TD([[makeQuery(id+"F13.imprint","IMPRINT",EDGE,{"derivedFrom":sQuery(id+"F13.wireOp",EDGE,"E48")}),1.0]])]});
            extrude(context, id + "F21", {"entities" : qUnion([Q0, Q1]), "oppositeDirection" : true, "depth" : 2.54 * mm, "offsetDistance" : 25.4 * mm});
        }
        {
            var Q0;
            Q0=makeQuery(id+"F15.imprint","IMPRINT",FACE,{"disambiguationData":[TD([[makeQuery(id+"F15.imprint","IMPRINT",EDGE,{"derivedFrom":sQuery(id+"F15.wireOp",EDGE,"E57")}),1.0]])]});
            var Q1;
            Q1=makeQuery(id+"F15.imprint","IMPRINT",FACE,{"disambiguationData":[TD([[makeQuery(id+"F15.imprint","IMPRINT",EDGE,{"derivedFrom":sQuery(id+"F15.wireOp",EDGE,"E58")}),1.0]])]});
            var Q2;
            Q2=makeQuery(id+"F15.imprint","IMPRINT",FACE,{"disambiguationData":[TD([[makeQuery(id+"F15.imprint","IMPRINT",EDGE,{"derivedFrom":sQuery(id+"F15.wireOp",EDGE,"E59")}),1.0]])]});
            var Q3;
            Q3=makeQuery(id+"F15.imprint","IMPRINT",FACE,{"disambiguationData":[TD([[makeQuery(id+"F15.imprint","IMPRINT",EDGE,{"derivedFrom":sQuery(id+"F15.wireOp",EDGE,"E60")}),1.0]])]});
            extrude(context, id + "F22", {"entities" : qUnion([Q0, Q1, Q2, Q3]), "oppositeDirection" : true, "depth" : 2.54 * mm, "offsetDistance" : 25.4 * mm});
        }
        {
            var Q0;
            Q0=makeQuery(id+"F17.imprint","IMPRINT",FACE,{"disambiguationData":[TD([[makeQuery(id+"F17.imprint","IMPRINT",EDGE,{"derivedFrom":sQuery(id+"F17.wireOp",EDGE,"E64")}),1.0]])]});
            extrude(context, id + "F23", {"entities" : qUnion([Q0]), "oppositeDirection" : true, "depth" : 2.54 * mm, "offsetDistance" : 25.4 * mm});
        }
        {
            var Q0;
            {var subQ0=sQuery(id+"F7.wireOp",EDGE,"E12");var subQ1=sQuery(id+"F7.wireOp",EDGE,"E9");var subQ2=makeQuery(id+"F7.imprint","INTERSECT",VERTEX,{"derivedFrom":[subQ1,subQ0]});Q0=makeQuery(id+"F7.imprint","IMPRINT",FACE,{"disambiguationData":[TD([[makeQuery(id+"F7.imprint","IMPRINT",EDGE,{"disambiguationData":[TD([[subQ2,1.0]])],"derivedFrom":subQ1}),-1.0]])]});}
            var Q1;
            {var subQ0=sQuery(id+"F7.wireOp",EDGE,"E12");var subQ1=sQuery(id+"F7.wireOp",EDGE,"E9");var subQ2=makeQuery(id+"F7.imprint","INTERSECT",VERTEX,{"derivedFrom":[subQ1,subQ0]});Q1=makeQuery(id+"F7.imprint","IMPRINT",FACE,{"disambiguationData":[TD([[makeQuery(id+"F7.imprint","IMPRINT",EDGE,{"disambiguationData":[TD([[subQ2,1.0]])],"derivedFrom":subQ1}),1.0]])]});}
            var Q2;
            Q2=makeQuery(id+"F7.imprint","IMPRINT",FACE,{"disambiguationData":[TD([[makeQuery(id+"F7.imprint","IMPRINT",EDGE,{"derivedFrom":sQuery(id+"F7.wireOp",EDGE,"E15")}),1.0]])]});
            var Q3;
            Q3=makeQuery(id+"F7.imprint","IMPRINT",FACE,{"disambiguationData":[TD([[makeQuery(id+"F7.imprint","IMPRINT",EDGE,{"derivedFrom":sQuery(id+"F7.wireOp",EDGE,"E16")}),1.0]])]});
            var Q4;
            Q4=makeQuery(id+"F7.imprint","IMPRINT",FACE,{"disambiguationData":[TD([[makeQuery(id+"F7.imprint","IMPRINT",EDGE,{"derivedFrom":sQuery(id+"F7.wireOp",EDGE,"E17")}),1.0]])]});
            var Q5;
            Q5=makeQuery(id+"F7.imprint","IMPRINT",FACE,{"disambiguationData":[TD([[makeQuery(id+"F7.imprint","IMPRINT",EDGE,{"derivedFrom":sQuery(id+"F7.wireOp",EDGE,"E18")}),1.0]])]});
            var Q6;
            {var subQ0=sQuery(id+"F7.wireOp",EDGE,"E13");var subQ1=sQuery(id+"F7.wireOp",EDGE,"E10");var subQ2=makeQuery(id+"F7.imprint","INTERSECT",VERTEX,{"derivedFrom":[subQ1,subQ0]});Q6=makeQuery(id+"F7.imprint","IMPRINT",FACE,{"disambiguationData":[TD([[makeQuery(id+"F7.imprint","IMPRINT",EDGE,{"disambiguationData":[TD([[subQ2,1.0]])],"derivedFrom":subQ1}),-1.0]])]});}
            var Q7;
            {var subQ0=sQuery(id+"F7.wireOp",EDGE,"E13");var subQ1=sQuery(id+"F7.wireOp",EDGE,"E10");var subQ2=makeQuery(id+"F7.imprint","INTERSECT",VERTEX,{"derivedFrom":[subQ1,subQ0]});Q7=makeQuery(id+"F7.imprint","IMPRINT",FACE,{"disambiguationData":[TD([[makeQuery(id+"F7.imprint","IMPRINT",EDGE,{"disambiguationData":[TD([[subQ2,1.0]])],"derivedFrom":subQ1}),1.0]])]});}
            extrude(context, id + "F24", {"entities" : qUnion([Q0, Q1, Q2, Q3, Q4, Q5, Q6, Q7]), "oppositeDirection" : true, "depth" : 2.54 * mm, "offsetDistance" : 25.4 * mm});
        }
    });
